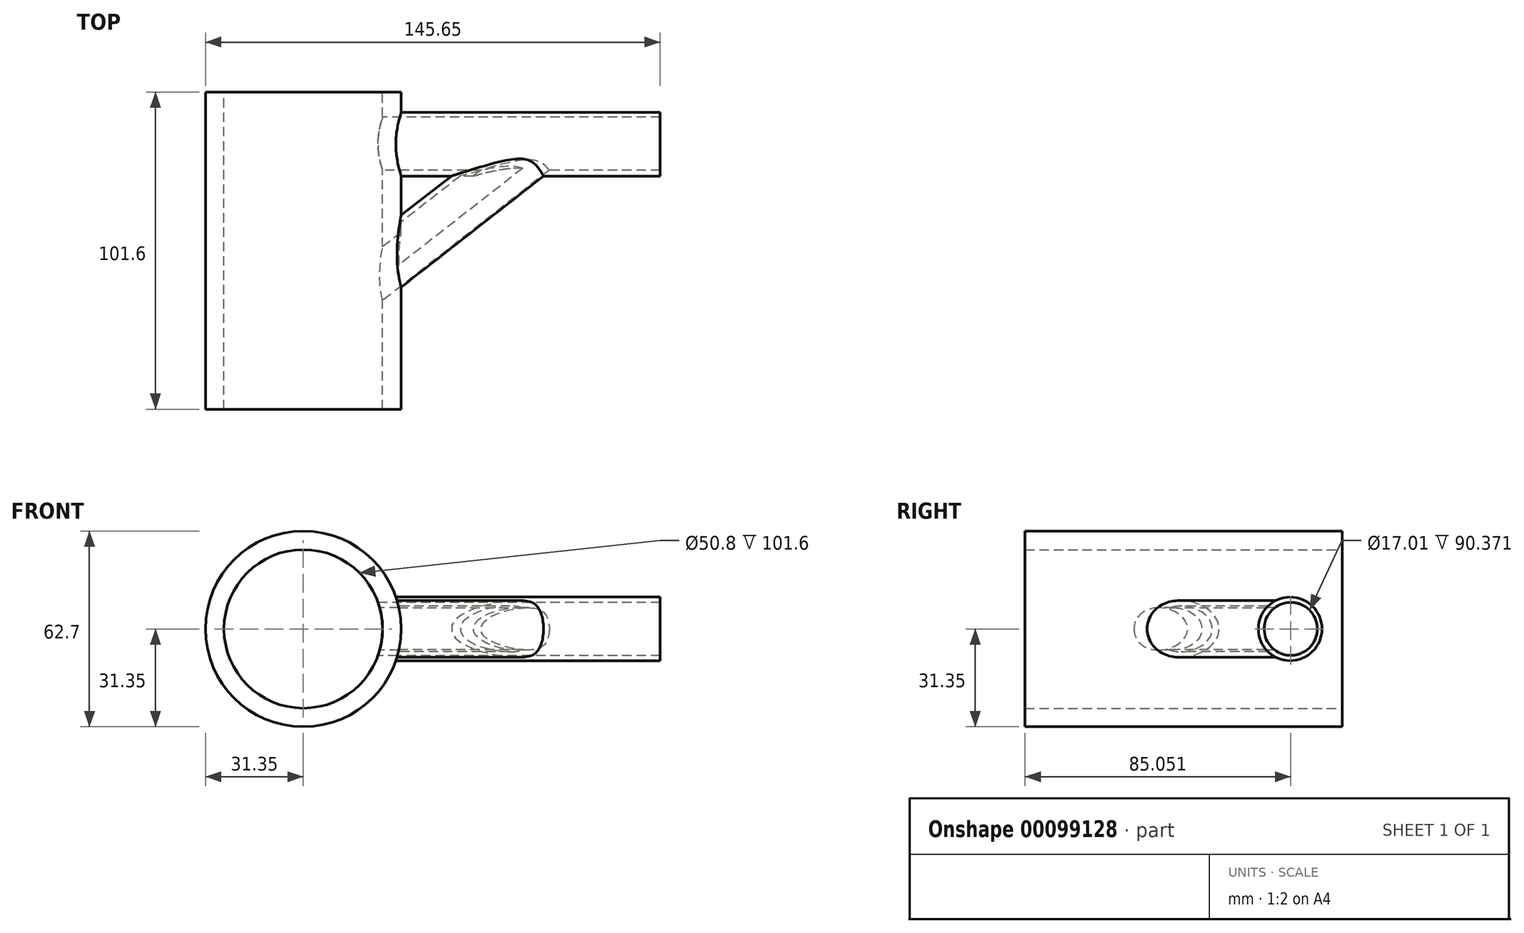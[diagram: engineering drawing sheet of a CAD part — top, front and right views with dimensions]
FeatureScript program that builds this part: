
annotation { "Feature Type Name" : "Feature", "Feature Type Description" : "" }
export const myFeature = defineFeature(function(context is Context, id is Id, definition is map)
    precondition{}
    {
        {
            var Q0;
            Q0=qCreatedBy(makeId("Front.planeOp"),FACE);
            var sketch = newSketch(context, id + "F0", { "sketchPlane" : qUnion([Q0])});
            skCircle(sketch, "E0", {"center": v(0, 0) * mm, "radius": 31.35 * mm});
            skSolve(sketch);
        }
        {
            var Q0;
            Q0=makeQuery(id+"F0.imprint","IMPRINT",FACE,{"disambiguationData":[TD([[makeQuery(id+"F0.imprint","IMPRINT",EDGE,{"derivedFrom":sQuery(id+"F0.wireOp",EDGE,"E0")}),1.0]])]});
            extrude(context, id + "F1", {"entities" : qUnion([Q0]), "depth" : 101.6 * mm});
        }
        {
            var Q0;
            Q0=makeQuery(id+"F1.opExtrude","CAP_FACE",FACE,{"disambiguationData":[OSD([sQuery(id+"F0.wireOp",EDGE,"E0")])],"isStart":true});
            var sketch = newSketch(context, id + "F2", { "sketchPlane" : qUnion([Q0])});
            skCircle(sketch, "E1", {"center": v(0, 0) * mm, "radius": 25.4 * mm});
            skSolve(sketch);
        }
        {
            var Q0;
            Q0=makeQuery(id+"F2.imprint","IMPRINT",FACE,{"disambiguationData":[TD([[makeQuery(id+"F2.imprint","IMPRINT",EDGE,{"derivedFrom":sQuery(id+"F2.wireOp",EDGE,"E1")}),1.0]])]});
            extrude(context, id + "F3", {"entities" : qUnion([Q0]), "operationType" : NewBodyOperationType.REMOVE, "oppositeDirection" : true, "depth" : 101.6 * mm});
        }
        {
            var Q0;
            Q0=qCreatedBy(makeId("Right.planeOp"),FACE);
            var sketch = newSketch(context, id + "F4", { "sketchPlane" : qUnion([Q0])});
            skCircle(sketch, "E2", {"center": v(-16.73, 0) * mm, "radius": 10.2 * mm});
            skSolve(sketch);
        }
        {
            var Q0;
            Q0 = qSketchRegion(id + "F4", true);
            extrude(context, id + "F5", {"entities" : qUnion([Q0]), "operationType" : NewBodyOperationType.ADD, "depth" : 114.3 * mm, "hasSecondDirection" : true, "secondDirectionOppositeDirection" : false, "secondDirectionDepth" : 25.4 * mm});
        }
        {
            var Q0;
            Q0=qCreatedBy(makeId("Right.planeOp"),FACE);
            var sketch = newSketch(context, id + "F6", { "sketchPlane" : qUnion([Q0])});
            skCircle(sketch, "E3", {"center": v(-16.55, 0) * mm, "radius": 8.5 * mm});
            skSolve(sketch);
        }
        {
            var Q0;
            Q0 = qSketchRegion(id + "F6", true);
            var Q1;
            Q1=makeQuery(id+"F5.opExtrude","CAP_FACE",FACE,{"disambiguationData":[OSD([sQuery(id+"F4.wireOp",EDGE,"E2")])],"isStart":false});
            extrude(context, id + "F7", {"entities" : qUnion([Q0, Q1]), "operationType" : NewBodyOperationType.REMOVE, "depth" : 127 * mm, "hasSecondDirection" : true, "secondDirectionOppositeDirection" : false, "secondDirectionDepth" : 12.7 * mm});
        }
        {
            var Q0;
            Q0=qCreatedBy(makeId("Top.planeOp"),FACE);
            var sketch = newSketch(context, id + "F8", { "sketchPlane" : qUnion([Q0])});
            skLineSegment(sketch, "E4", {"start": v(0, -59.19) * mm, "end": v(13.78, -76.83) * mm});
            skLineSegment(sketch, "E5", {"start": v(13.78, -76.83) * mm, "end": v(26.81, -66.65) * mm});
            skLineSegment(sketch, "E6", {"start": v(26.81, -66.65) * mm, "end": v(11.7, -47.32) * mm});
            skLineSegment(sketch, "E7", {"start": v(11.7, -47.32) * mm, "end": v(0, -59.19) * mm});
            skSolve(sketch);
        }
        {
            var Q0;
            Q0 = qSketchRegion(id + "F8", true);
            extrude(context, id + "F9", {"entities" : qUnion([Q0]), "operationType" : NewBodyOperationType.ADD, "endBound" : BoundingType.SYMMETRIC, "depth" : 25.4 * mm});
        }
        {
            var Q0;
            Q0=makeQuery(id+"F9.opExtrude","SWEPT_FACE",FACE,{"disambiguationData":[OSD([sQuery(id+"F8.wireOp",EDGE,"E4")])]});
            var sketch = newSketch(context, id + "F10", { "sketchPlane" : qUnion([Q0])});
            skCircle(sketch, "E8", {"center": v(59.48, 0) * mm, "radius": 9.08 * mm});
            skCircle(sketch, "E9", {"center": v(59.48, 0) * mm, "radius": 7.33 * mm});
            skSolve(sketch);
        }
        {
            var Q0;
            Q0 = qSketchRegion(id + "F10", true);
            var Q1;
            Q1=makeQuery(id+"F5.opExtrude","SWEPT_FACE",FACE,{"disambiguationData":[OSD([sQuery(id+"F4.wireOp",EDGE,"E2")])]});
            var Q2;
            Q2=makeQuery(id+"F1.opExtrude","SWEPT_FACE",FACE,{"disambiguationData":[OSD([sQuery(id+"F0.wireOp",EDGE,"E0")])]});
            extrude(context, id + "F11", {"entities" : qUnion([Q0]), "operationType" : NewBodyOperationType.ADD, "endBound" : BoundingType.UP_TO_SURFACE, "oppositeDirection" : true, "endBoundEntityFace" : qUnion([Q1]), "depth" : 86.36 * mm, "hasSecondDirection" : true, "secondDirectionBound" : SecondDirectionBoundingType.UP_TO_SURFACE, "secondDirectionOppositeDirection" : true, "secondDirectionBoundEntityFace" : qUnion([Q2]), "secondDirectionDepth" : 25.4 * mm});
        }
        {
            var Q0;
            Q0=makeQuery(id+"F9.opExtrude","SWEPT_FACE",FACE,{"disambiguationData":[OSD([sQuery(id+"F8.wireOp",EDGE,"E4")])]});
            var sketch = newSketch(context, id + "F12", { "sketchPlane" : qUnion([Q0])});
            skCircle(sketch, "E10", {"center": v(61.48, 0) * mm, "radius": 6.76 * mm});
            skSolve(sketch);
        }
        {
            var Q0;
            Q0=makeQuery(id+"F12.imprint","IMPRINT",FACE,{"disambiguationData":[TD([[makeQuery(id+"F12.imprint","IMPRINT",EDGE,{"derivedFrom":sQuery(id+"F12.wireOp",EDGE,"E10")}),1.0]])]});
            extrude(context, id + "F13", {"entities" : qUnion([Q0]), "operationType" : NewBodyOperationType.REMOVE, "oppositeDirection" : true, "depth" : 86.36 * mm});
        }
        {
            var Q0;
            Q0=qCreatedBy(makeId("Front.planeOp"),FACE);
            var sketch = newSketch(context, id + "F14", { "sketchPlane" : qUnion([Q0])});
            skCircle(sketch, "E11", {"center": v(0, 0) * mm, "radius": 25.4 * mm});
            skSolve(sketch);
        }
        {
            var Q0;
            Q0=makeQuery(id+"F14.imprint","IMPRINT",FACE,{"disambiguationData":[TD([[makeQuery(id+"F14.imprint","IMPRINT",EDGE,{"derivedFrom":sQuery(id+"F14.wireOp",EDGE,"E11")}),1.0]])]});
            extrude(context, id + "F15", {"entities" : qUnion([Q0]), "operationType" : NewBodyOperationType.REMOVE, "endBound" : BoundingType.THROUGH_ALL, "depth" : 25.4 * mm});
        }
    });
